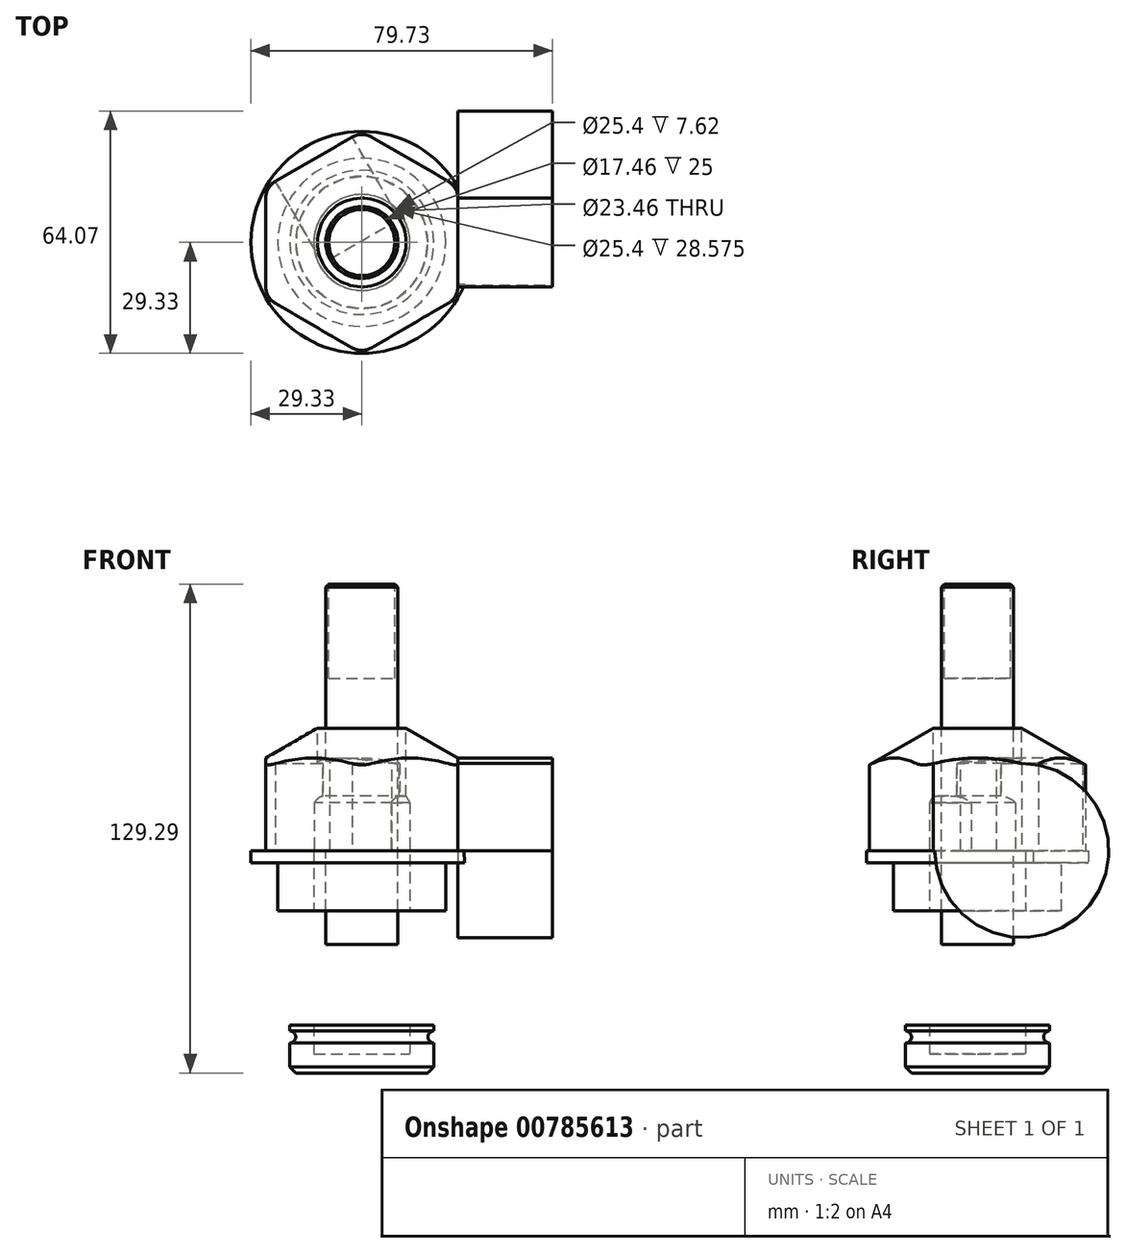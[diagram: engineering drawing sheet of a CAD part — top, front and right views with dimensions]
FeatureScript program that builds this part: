
annotation { "Feature Type Name" : "Feature", "Feature Type Description" : "" }
export const myFeature = defineFeature(function(context is Context, id is Id, definition is map)
    precondition{}
    {
        {
            var Q0;
            Q0=qCreatedBy(makeId("Top.planeOp"),FACE);
            var sketch = newSketch(context, id + "F0", { "sketchPlane" : qUnion([Q0])});
            skCircle(sketch, "E0", {"center": v(0, 0) * mm, "radius": 29.33 * mm});
            skLineSegment(sketch, "E1", {"start": v(0, 29.33) * mm, "end": v(0, -29.33) * mm, "construction": true});
            skLineSegment(sketch, "E2", {"start": v(-25.4, 14.66) * mm, "end": v(25.4, -14.66) * mm, "construction": true});
            skLineSegment(sketch, "E3", {"start": v(-25.4, -14.66) * mm, "end": v(25.4, 14.66) * mm, "construction": true});
            skLineSegment(sketch, "E4", {"start": v(-25.4, 14.66) * mm, "end": v(0, 29.33) * mm});
            skLineSegment(sketch, "E5", {"start": v(0, 29.33) * mm, "end": v(25.4, 14.66) * mm});
            skLineSegment(sketch, "E6", {"start": v(25.4, 14.66) * mm, "end": v(25.4, -14.66) * mm});
            skLineSegment(sketch, "E7", {"start": v(25.4, -14.66) * mm, "end": v(0, -29.33) * mm});
            skLineSegment(sketch, "E8", {"start": v(0, -29.33) * mm, "end": v(-25.4, -14.66) * mm});
            skLineSegment(sketch, "E9", {"start": v(-25.4, -14.66) * mm, "end": v(-25.4, 14.66) * mm});
            skCircle(sketch, "E10", {"center": v(0, 0) * mm, "radius": 7.94 * mm});
            skSolve(sketch);
        }
        {
            var Q0;
            Q0=makeQuery(id+"F0.imprint","IMPRINT",FACE,{"disambiguationData":[TD([[makeQuery(id+"F0.imprint","IMPRINT",EDGE,{"derivedFrom":sQuery(id+"F0.wireOp",EDGE,"E10")}),1.0]])]});
            var Q1;
            Q1=makeQuery(id+"F0.imprint","IMPRINT",FACE,{"disambiguationData":[TD([[makeQuery(id+"F0.imprint","IMPRINT",EDGE,{"derivedFrom":sQuery(id+"F0.wireOp",EDGE,"E4")}),-1.0]])]});
            extrude(context, id + "F1", {"entities" : qUnion([Q0, Q1]), "depth" : 35.56 * mm});
        }
        {
            var Q0;
            {var subQ0=sQuery(id+"F0.wireOp",EDGE,"E8");Q0=makeQuery(id+"F0.imprint","IMPRINT",FACE,{"disambiguationData":[TD([[makeQuery(id+"F0.imprint","IMPRINT",EDGE,{"derivedFrom":subQ0}),1.0]])]});}
            var Q1;
            {var subQ0=sQuery(id+"F0.wireOp",EDGE,"E7");Q1=makeQuery(id+"F0.imprint","IMPRINT",FACE,{"disambiguationData":[TD([[makeQuery(id+"F0.imprint","IMPRINT",EDGE,{"derivedFrom":subQ0}),1.0]])]});}
            var Q2;
            {var subQ0=sQuery(id+"F0.wireOp",EDGE,"E6");Q2=makeQuery(id+"F0.imprint","IMPRINT",FACE,{"disambiguationData":[TD([[makeQuery(id+"F0.imprint","IMPRINT",EDGE,{"derivedFrom":subQ0}),1.0]])]});}
            var Q3;
            Q3=makeQuery(id+"F0.imprint","IMPRINT",FACE,{"disambiguationData":[TD([[makeQuery(id+"F0.imprint","IMPRINT",EDGE,{"derivedFrom":sQuery(id+"F0.wireOp",EDGE,"E4")}),-1.0]])]});
            var Q4;
            {var subQ0=sQuery(id+"F0.wireOp",EDGE,"E5");Q4=makeQuery(id+"F0.imprint","IMPRINT",FACE,{"disambiguationData":[TD([[makeQuery(id+"F0.imprint","IMPRINT",EDGE,{"derivedFrom":subQ0}),1.0]])]});}
            var Q5;
            {var subQ0=sQuery(id+"F0.wireOp",EDGE,"E4");Q5=makeQuery(id+"F0.imprint","IMPRINT",FACE,{"disambiguationData":[TD([[makeQuery(id+"F0.imprint","IMPRINT",EDGE,{"derivedFrom":subQ0}),1.0]])]});}
            var Q6;
            {var subQ0=sQuery(id+"F0.wireOp",EDGE,"E9");Q6=makeQuery(id+"F0.imprint","IMPRINT",FACE,{"disambiguationData":[TD([[makeQuery(id+"F0.imprint","IMPRINT",EDGE,{"derivedFrom":subQ0}),1.0]])]});}
            extrude(context, id + "F2", {"entities" : qUnion([Q0, Q1, Q2, Q3, Q4, Q5, Q6]), "operationType" : NewBodyOperationType.ADD, "depth" : 3.17 * mm});
        }
        {
            var Q0;
            Q0=makeQuery(id+"F1.opExtrude","SWEPT_EDGE",EDGE,{"disambiguationData":[OSD([sQuery(id+"F0.wireOp",EDGE,"E0"),sQuery(id+"F0.wireOp",EDGE,"E7"),sQuery(id+"F0.wireOp",EDGE,"E8")])]});
            var Q1;
            Q1=makeQuery(id+"F1.opExtrude","SWEPT_EDGE",EDGE,{"disambiguationData":[OSD([sQuery(id+"F0.wireOp",EDGE,"E0"),sQuery(id+"F0.wireOp",EDGE,"E6"),sQuery(id+"F0.wireOp",EDGE,"E7")])]});
            var Q2;
            Q2=makeQuery(id+"F1.opExtrude","SWEPT_EDGE",EDGE,{"disambiguationData":[OSD([sQuery(id+"F0.wireOp",EDGE,"E0"),sQuery(id+"F0.wireOp",EDGE,"E5"),sQuery(id+"F0.wireOp",EDGE,"E6")])]});
            var Q3;
            Q3=makeQuery(id+"F1.opExtrude","SWEPT_EDGE",EDGE,{"disambiguationData":[OSD([sQuery(id+"F0.wireOp",EDGE,"E0"),sQuery(id+"F0.wireOp",EDGE,"E4"),sQuery(id+"F0.wireOp",EDGE,"E5")])]});
            var Q4;
            Q4=makeQuery(id+"F1.opExtrude","SWEPT_EDGE",EDGE,{"disambiguationData":[OSD([sQuery(id+"F0.wireOp",EDGE,"E0"),sQuery(id+"F0.wireOp",EDGE,"E4"),sQuery(id+"F0.wireOp",EDGE,"E9")])]});
            var Q5;
            Q5=makeQuery(id+"F1.opExtrude","SWEPT_EDGE",EDGE,{"disambiguationData":[OSD([sQuery(id+"F0.wireOp",EDGE,"E0"),sQuery(id+"F0.wireOp",EDGE,"E8"),sQuery(id+"F0.wireOp",EDGE,"E9")])]});
            fillet(context, id + "F3", {"entities" : qUnion([Q0, Q1, Q2, Q3, Q4, Q5]), "radius" : 5.08 * mm, "tangentPropagation" : true, "allowEdgeOverflow" : false});
        }
        {
            var Q0;
            Q0=qCreatedBy(makeId("Right.planeOp"),FACE);
            var sketch = newSketch(context, id + "F4", { "sketchPlane" : qUnion([Q0])});
            skLineSegment(sketch, "E11", {"start": v(0, 52) * mm, "end": v(0, 0) * mm, "construction": true});
            skLineSegment(sketch, "E12", {"start": v(11.73, 35.56) * mm, "end": v(35.4, 21.9) * mm});
            skLineSegment(sketch, "E13", {"start": v(35.4, 21.9) * mm, "end": v(35.4, 35.56) * mm});
            skLineSegment(sketch, "E14", {"start": v(35.4, 35.56) * mm, "end": v(11.73, 35.56) * mm});
            skLineSegment(sketch, "E15.0", {"start": v(11.73, 35.56) * mm, "end": v(-11.73, 35.56) * mm});
            skLineSegment(sketch, "E16.bottom", {"start": v(0, 0) * mm, "end": v(22.23, 0) * mm});
            skLineSegment(sketch, "E16.top", {"start": v(0, -12.7) * mm, "end": v(22.23, -12.7) * mm});
            skLineSegment(sketch, "E16.left", {"start": v(0, 0) * mm, "end": v(0, -12.7) * mm});
            skLineSegment(sketch, "E16.right", {"start": v(22.23, 0) * mm, "end": v(22.23, -12.7) * mm});
            skLineSegment(sketch, "E17.bottom", {"start": v(0, -12.7) * mm, "end": v(19.05, -12.7) * mm});
            skLineSegment(sketch, "E17.top", {"start": v(0, -27.69) * mm, "end": v(19.05, -27.69) * mm});
            skLineSegment(sketch, "E17.left", {"start": v(0, -12.7) * mm, "end": v(0, -27.69) * mm});
            skLineSegment(sketch, "E17.right", {"start": v(19.05, -12.7) * mm, "end": v(19.05, -27.69) * mm});
            skLineSegment(sketch, "E18.bottom", {"start": v(17.78, -27.69) * mm, "end": v(0, -27.69) * mm});
            skLineSegment(sketch, "E18.top", {"start": v(17.78, -42.93) * mm, "end": v(0, -42.93) * mm});
            skLineSegment(sketch, "E18.left", {"start": v(17.78, -27.69) * mm, "end": v(17.78, -42.93) * mm});
            skLineSegment(sketch, "E18.right", {"start": v(0, -27.69) * mm, "end": v(0, -42.93) * mm});
            skLineSegment(sketch, "E19.bottom", {"start": v(0, -42.93) * mm, "end": v(19.05, -42.93) * mm});
            skLineSegment(sketch, "E19.top", {"start": v(0, -55.63) * mm, "end": v(19.05, -55.63) * mm});
            skLineSegment(sketch, "E19.left", {"start": v(0, -42.93) * mm, "end": v(0, -55.63) * mm});
            skLineSegment(sketch, "E19.right", {"start": v(19.05, -42.93) * mm, "end": v(19.05, -55.63) * mm});
            skCircle(sketch, "E20", {"center": v(19.05, -24.51) * mm, "radius": 1.59 * mm});
            skCircle(sketch, "E21", {"center": v(19.05, -46.1) * mm, "radius": 1.59 * mm});
            skCircle(sketch, "E22", {"center": v(0, -17.46) * mm, "radius": 3.18 * mm});
            skCircle(sketch, "E23", {"center": v(0, -35.3) * mm, "radius": 3.18 * mm});
            skSolve(sketch);
        }
        {
            var Q0;
            Q0=makeQuery(id+"F4.imprint","IMPRINT",FACE,{"disambiguationData":[TD([[makeQuery(id+"F4.imprint","IMPRINT",EDGE,{"derivedFrom":sQuery(id+"F4.wireOp",EDGE,"E12")}),1.0]])]});
            var Q1;
            Q1=sQuery(id+"F4.wireOp",EDGE,"E11");
            revolve(context, id + "F5", {"operationType" : NewBodyOperationType.REMOVE, "entities" : qUnion([Q0]), "axis" : qUnion([Q1]), "revolveType" : RevolveType.FULL, "oppositeDirection" : true});
        }
        {
            var Q0;
            {var subQ7=sQuery(id+"F4.wireOp",EDGE,"E18.bottom");Q0=makeQuery(id+"F4.imprint","IMPRINT",FACE,{"disambiguationData":[TD([[makeQuery(id+"F4.imprint","IMPRINT",EDGE,{"derivedFrom":subQ7}),1.0]])]});}
            var Q1;
            {var subQ10=sQuery(id+"F4.wireOp",EDGE,"E17.bottom");Q1=makeQuery(id+"F4.imprint","IMPRINT",FACE,{"disambiguationData":[TD([[makeQuery(id+"F4.imprint","IMPRINT",EDGE,{"derivedFrom":subQ10}),-1.0]])]});}
            var Q2;
            Q2=makeQuery(id+"F4.imprint","IMPRINT",FACE,{"disambiguationData":[TD([[makeQuery(id+"F4.imprint","IMPRINT",EDGE,{"derivedFrom":sQuery(id+"F4.wireOp",EDGE,"E16.bottom")}),-1.0]])]});
            var Q3;
            {var subQ4=sQuery(id+"F4.wireOp",EDGE,"E19.top");Q3=makeQuery(id+"F4.imprint","IMPRINT",FACE,{"disambiguationData":[TD([[makeQuery(id+"F4.imprint","IMPRINT",EDGE,{"derivedFrom":subQ4}),1.0]])]});}
            var Q4;
            Q4=sQuery(id+"F4.wireOp",EDGE,"E11");
            revolve(context, id + "F6", {"operationType" : NewBodyOperationType.ADD, "entities" : qUnion([Q0, Q1, Q2, Q3]), "axis" : qUnion([Q4]), "revolveType" : RevolveType.FULL});
        }
        {
            var Q0;
            Q0=makeQuery(id+"F6.opRevolve","SWEPT_EDGE",EDGE,{"disambiguationData":[OSD([sQuery(id+"F4.wireOp",EDGE,"E19.top"),sQuery(id+"F4.wireOp",EDGE,"E19.right")])]});
            chamfer(context, id + "F7", {"entities" : qUnion([Q0]), "width" : 1.59 * mm, "tangentPropagation" : true});
        }
        {
            var Q0;
            {var subQ0=sQuery(id+"F4.wireOp",EDGE,"E16.right");var subQ1=sQuery(id+"F4.wireOp",EDGE,"E20");var subQ3=makeQuery(id+"F4.imprint","INTERSECT",VERTEX,{"disambiguationData":[OD(0.0)],"derivedFrom":[subQ0,subQ1]});Q0=makeQuery(id+"F4.imprint","IMPRINT",FACE,{"disambiguationData":[TD([[makeQuery(id+"F4.imprint","SKETCH_ENTITY",EDGE,{"disambiguationData":[TD([[subQ3,-1.0]])],"sketchEntityId":"E16.right"}),1.0]])]});}
            var Q1;
            {var subQ0=sQuery(id+"F4.wireOp",EDGE,"E20");var subQ1=sQuery(id+"F4.wireOp",EDGE,"E17.right");var subQ3=makeQuery(id+"F4.imprint","INTERSECT",VERTEX,{"disambiguationData":[OD(0.0)],"derivedFrom":[subQ1,subQ0]});Q1=makeQuery(id+"F4.imprint","IMPRINT",FACE,{"disambiguationData":[TD([[makeQuery(id+"F4.imprint","IMPRINT",EDGE,{"disambiguationData":[TD([[subQ3,-1.0]])],"derivedFrom":subQ1}),-1.0]])]});}
            var Q2;
            {var subQ0=sQuery(id+"F4.wireOp",EDGE,"E20");var subQ1=sQuery(id+"F4.wireOp",EDGE,"E17.right");var subQ3=makeQuery(id+"F4.imprint","INTERSECT",VERTEX,{"disambiguationData":[OD(0.0)],"derivedFrom":[subQ1,subQ0]});Q2=makeQuery(id+"F4.imprint","IMPRINT",FACE,{"disambiguationData":[TD([[makeQuery(id+"F4.imprint","IMPRINT",EDGE,{"disambiguationData":[TD([[subQ3,-1.0]])],"derivedFrom":subQ1}),1.0]])]});}
            var Q3;
            Q3=sQuery(id+"F4.wireOp",EDGE,"E11");
            revolve(context, id + "F8", {"entities" : qUnion([Q0, Q1, Q2]), "axis" : qUnion([Q3]), "revolveType" : RevolveType.FULL});
        }
        {
            var Q0;
            {var subQ0=sQuery(id+"F4.wireOp",EDGE,"E22");var subQ1=sQuery(id+"F4.wireOp",EDGE,"E17.left");var subQ3=makeQuery(id+"F4.imprint","INTERSECT",VERTEX,{"disambiguationData":[OD(0.0)],"derivedFrom":[subQ1,subQ0]});Q0=makeQuery(id+"F4.imprint","IMPRINT",FACE,{"disambiguationData":[TD([[makeQuery(id+"F4.imprint","IMPRINT",EDGE,{"disambiguationData":[TD([[subQ3,-1.0]])],"derivedFrom":subQ1}),-1.0]])]});}
            var Q1;
            {var subQ0=sQuery(id+"F4.wireOp",EDGE,"E22");var subQ1=sQuery(id+"F4.wireOp",EDGE,"E17.left");var subQ3=makeQuery(id+"F4.imprint","INTERSECT",VERTEX,{"disambiguationData":[OD(0.0)],"derivedFrom":[subQ1,subQ0]});Q1=makeQuery(id+"F4.imprint","IMPRINT",FACE,{"disambiguationData":[TD([[makeQuery(id+"F4.imprint","IMPRINT",EDGE,{"disambiguationData":[TD([[subQ3,-1.0]])],"derivedFrom":subQ1}),1.0]])]});}
            var Q2;
            {var subQ0=sQuery(id+"F4.wireOp",EDGE,"E23");var subQ1=sQuery(id+"F4.wireOp",EDGE,"E18.right");var subQ3=makeQuery(id+"F4.imprint","INTERSECT",VERTEX,{"disambiguationData":[OD(0.0)],"derivedFrom":[subQ1,subQ0]});Q2=makeQuery(id+"F4.imprint","IMPRINT",FACE,{"disambiguationData":[TD([[makeQuery(id+"F4.imprint","IMPRINT",EDGE,{"disambiguationData":[TD([[subQ3,-1.0]])],"derivedFrom":subQ1}),-1.0]])]});}
            var Q3;
            {var subQ0=sQuery(id+"F4.wireOp",EDGE,"E23");var subQ1=sQuery(id+"F4.wireOp",EDGE,"E18.right");var subQ3=makeQuery(id+"F4.imprint","INTERSECT",VERTEX,{"disambiguationData":[OD(0.0)],"derivedFrom":[subQ1,subQ0]});Q3=makeQuery(id+"F4.imprint","IMPRINT",FACE,{"disambiguationData":[TD([[makeQuery(id+"F4.imprint","IMPRINT",EDGE,{"disambiguationData":[TD([[subQ3,-1.0]])],"derivedFrom":subQ1}),1.0]])]});}
            extrude(context, id + "F9", {"entities" : qUnion([Q0, Q1, Q2, Q3]), "operationType" : NewBodyOperationType.REMOVE, "endBound" : BoundingType.THROUGH_ALL, "depth" : 25.4 * mm});
        }
        {
            var Q0;
            Q0=qCreatedBy(makeId("Right.planeOp"),FACE);
            var sketch = newSketch(context, id + "F10", { "sketchPlane" : qUnion([Q0])});
            skLineSegment(sketch, "E24", {"start": v(0, 73.66) * mm, "end": v(0, -50.55) * mm});
            skLineSegment(sketch, "E25", {"start": v(0, -50.55) * mm, "end": v(12.7, -50.55) * mm});
            skLineSegment(sketch, "E26", {"start": v(12.7, -50.55) * mm, "end": v(12.7, 15.88) * mm});
            skLineSegment(sketch, "E27", {"start": v(12.7, 15.88) * mm, "end": v(0, 15.88) * mm});
            skLineSegment(sketch, "E28", {"start": v(9.53, -21.6) * mm, "end": v(9.53, 73.66) * mm});
            skLineSegment(sketch, "E29", {"start": v(9.52, 73.66) * mm, "end": v(0, 73.66) * mm});
            skLineSegment(sketch, "E30", {"start": v(9.53, 21.37) * mm, "end": v(12.7, 15.88) * mm});
            skLineSegment(sketch, "E31.rect.bottom", {"start": v(12.7, -27.94) * mm, "end": v(-12.7, -27.94) * mm});
            skLineSegment(sketch, "E31.rect.top", {"start": v(12.7, -21.59) * mm, "end": v(-12.7, -21.59) * mm});
            skLineSegment(sketch, "E31.rect.left", {"start": v(12.7, -27.94) * mm, "end": v(12.7, -21.59) * mm});
            skLineSegment(sketch, "E31.rect.right", {"start": v(-12.7, -27.94) * mm, "end": v(-12.7, -21.59) * mm});
            skPoint(sketch, "E31.rect.middle", {"position": v(0, -24.77) * mm});
            skSolve(sketch);
        }
        {
            var Q0;
            {var subQ0=sQuery(id+"F10.wireOp",EDGE,"E29");Q0=makeQuery(id+"F10.imprint","IMPRINT",FACE,{"disambiguationData":[TD([[makeQuery(id+"F10.imprint","IMPRINT",EDGE,{"derivedFrom":subQ0}),1.0]])]});}
            var Q1;
            {var subQ0=sQuery(id+"F10.wireOp",EDGE,"E30");Q1=makeQuery(id+"F10.imprint","IMPRINT",FACE,{"disambiguationData":[TD([[makeQuery(id+"F10.imprint","IMPRINT",EDGE,{"derivedFrom":subQ0}),-1.0]])]});}
            var Q2;
            {var subQ1=sQuery(id+"F10.wireOp",EDGE,"E24");var subQ5=sQuery(id+"F10.wireOp",EDGE,"E27");var subQ7=makeQuery(id+"F10.imprint","INTERSECT",VERTEX,{"derivedFrom":[subQ1,subQ5]});Q2=makeQuery(id+"F10.imprint","IMPRINT",FACE,{"disambiguationData":[TD([[makeQuery(id+"F10.imprint","IMPRINT",EDGE,{"disambiguationData":[TD([[subQ7,-1.0]])],"derivedFrom":subQ1}),1.0]])]});}
            var Q3;
            {var subQ0=sQuery(id+"F10.wireOp",EDGE,"E31.rect.top");var subQ3=sQuery(id+"F10.wireOp",EDGE,"E28");var subQ4=makeQuery(id+"F10.imprint","INTERSECT",VERTEX,{"derivedFrom":[subQ3,subQ0]});Q3=makeQuery(id+"F10.imprint","IMPRINT",FACE,{"disambiguationData":[TD([[makeQuery(id+"F10.imprint","IMPRINT",EDGE,{"disambiguationData":[TD([[subQ4,-1.0]])],"derivedFrom":subQ3}),-1.0]])]});}
            var Q4;
            {var subQ5=sQuery(id+"F10.wireOp",EDGE,"E25");Q4=makeQuery(id+"F10.imprint","IMPRINT",FACE,{"disambiguationData":[TD([[makeQuery(id+"F10.imprint","IMPRINT",EDGE,{"derivedFrom":subQ5}),1.0]])]});}
            var Q5;
            {var subQ0=sQuery(id+"F10.wireOp",EDGE,"E31.rect.left");Q5=makeQuery(id+"F10.imprint","IMPRINT",FACE,{"disambiguationData":[TD([[makeQuery(id+"F10.imprint","IMPRINT",EDGE,{"derivedFrom":subQ0}),1.0]])]});}
            var Q6;
            Q6=sQuery(id+"F10.wireOp",EDGE,"E24");
            revolve(context, id + "F11", {"operationType" : NewBodyOperationType.REMOVE, "entities" : qUnion([Q0, Q1, Q2, Q3, Q4, Q5]), "axis" : qUnion([Q6]), "revolveType" : RevolveType.FULL, "oppositeDirection" : true});
        }
        {
            var Q0;
            {var subQ0=sQuery(id+"F10.wireOp",EDGE,"E29");Q0=makeQuery(id+"F10.imprint","IMPRINT",FACE,{"disambiguationData":[TD([[makeQuery(id+"F10.imprint","IMPRINT",EDGE,{"derivedFrom":subQ0}),1.0]])]});}
            var Q1;
            {var subQ1=sQuery(id+"F10.wireOp",EDGE,"E24");var subQ5=sQuery(id+"F10.wireOp",EDGE,"E27");var subQ7=makeQuery(id+"F10.imprint","INTERSECT",VERTEX,{"derivedFrom":[subQ1,subQ5]});Q1=makeQuery(id+"F10.imprint","IMPRINT",FACE,{"disambiguationData":[TD([[makeQuery(id+"F10.imprint","IMPRINT",EDGE,{"disambiguationData":[TD([[subQ7,-1.0]])],"derivedFrom":subQ1}),1.0]])]});}
            var Q2;
            {var subQ0=sQuery(id+"F10.wireOp",EDGE,"E31.rect.left");Q2=makeQuery(id+"F10.imprint","IMPRINT",FACE,{"disambiguationData":[TD([[makeQuery(id+"F10.imprint","IMPRINT",EDGE,{"derivedFrom":subQ0}),1.0]])]});}
            var Q3;
            Q3=sQuery(id+"F10.wireOp",EDGE,"E24");
            revolve(context, id + "F12", {"entities" : qUnion([Q0, Q1, Q2]), "axis" : qUnion([Q3]), "revolveType" : RevolveType.FULL});
        }
        {
            var Q0;
            Q0=makeQuery(id+"F12.opRevolve","SWEPT_EDGE",EDGE,{"disambiguationData":[OSD([sQuery(id+"F10.wireOp",EDGE,"E28"),sQuery(id+"F10.wireOp",EDGE,"E29")])]});
            chamfer(context, id + "F13", {"entities" : qUnion([Q0]), "width" : 0.8 * mm, "tangentPropagation" : true});
        }
        {
            var Q0;
            Q0=makeQuery(id+"F12.opRevolve","SWEPT_FACE",FACE,{"disambiguationData":[OSD([sQuery(id+"F10.wireOp",EDGE,"E29")])]});
            extrude(context, id + "F14", {"entities" : qUnion([Q0]), "operationType" : NewBodyOperationType.REMOVE, "oppositeDirection" : true, "depth" : 25 * mm, "offsetDistance" : 25 * mm});
        }
        {
            var Q0;
            Q0=makeQuery(id+"F1.opExtrude","CAP_FACE",FACE,{"disambiguationData":[OSD([sQuery(id+"F0.wireOp",EDGE,"E4"),sQuery(id+"F0.wireOp",EDGE,"E5"),sQuery(id+"F0.wireOp",EDGE,"E6"),sQuery(id+"F0.wireOp",EDGE,"E7"),sQuery(id+"F0.wireOp",EDGE,"E8"),sQuery(id+"F0.wireOp",EDGE,"E9")])],"isStart":false});
            extrude(context, id + "F15", {"entities" : qUnion([Q0]), "operationType" : NewBodyOperationType.REMOVE, "oppositeDirection" : true, "depth" : 25 * mm, "offsetDistance" : 25 * mm});
        }
        {
            var Q0;
            Q0=makeQuery(id+"F1.opExtrude","SWEPT_FACE",FACE,{"disambiguationData":[OSD([sQuery(id+"F0.wireOp",EDGE,"E4")])]});
            extrude(context, id + "F16", {"entities" : qUnion([Q0]), "operationType" : NewBodyOperationType.REMOVE, "oppositeDirection" : true, "depth" : 25 * mm, "offsetDistance" : 25 * mm});
        }
        {
            var Q0;
            Q0=makeQuery(id+"F1.opExtrude","SWEPT_FACE",FACE,{"disambiguationData":[OSD([sQuery(id+"F0.wireOp",EDGE,"E6")])]});
            extrude(context, id + "F17", {"entities" : qUnion([Q0]), "operationType" : NewBodyOperationType.ADD, "depth" : 25 * mm, "offsetDistance" : 25 * mm});
        }
        {
            var Q0;
            Q0=makeQuery(id+"F17.opExtrude","SWEPT_FACE",FACE,{"disambiguationData":[OSD([sQuery(id+"F0.wireOp",EDGE,"E0"),sQuery(id+"F0.wireOp",EDGE,"E5"),sQuery(id+"F0.wireOp",EDGE,"E6")])]});
            var Q1;
            {var subQ0=sQuery(id+"F0.wireOp",EDGE,"E10");var subQ1=sQuery(id+"F0.wireOp",EDGE,"E6");var subQ2=sQuery(id+"F0.wireOp",EDGE,"E0");var subQ3=sQuery(id+"F0.wireOp",EDGE,"E5");Q1=makeQuery(id+"F17.boolean.opBoolean","SPLIT",EDGE,{"disambiguationData":[topologyDisambiguationEdgeConnected([makeQuery(id+"F17.opExtrude","SWEPT_FACE",FACE,{"disambiguationData":[OSD([subQ2,subQ1,subQ0])]})])],"derivedFrom":makeQuery(id+"F17.opExtrude","SWEPT_EDGE",EDGE,{"disambiguationData":[OSD([subQ2,subQ3,subQ1,subQ0])]})});}
            revolve(context, id + "F18", {"operationType" : NewBodyOperationType.ADD, "surfaceOperationType" : NewSurfaceOperationType.NEW, "entities" : qUnion([Q0]), "axis" : qUnion([Q1]), "revolveType" : RevolveType.FULL});
        }
    });
